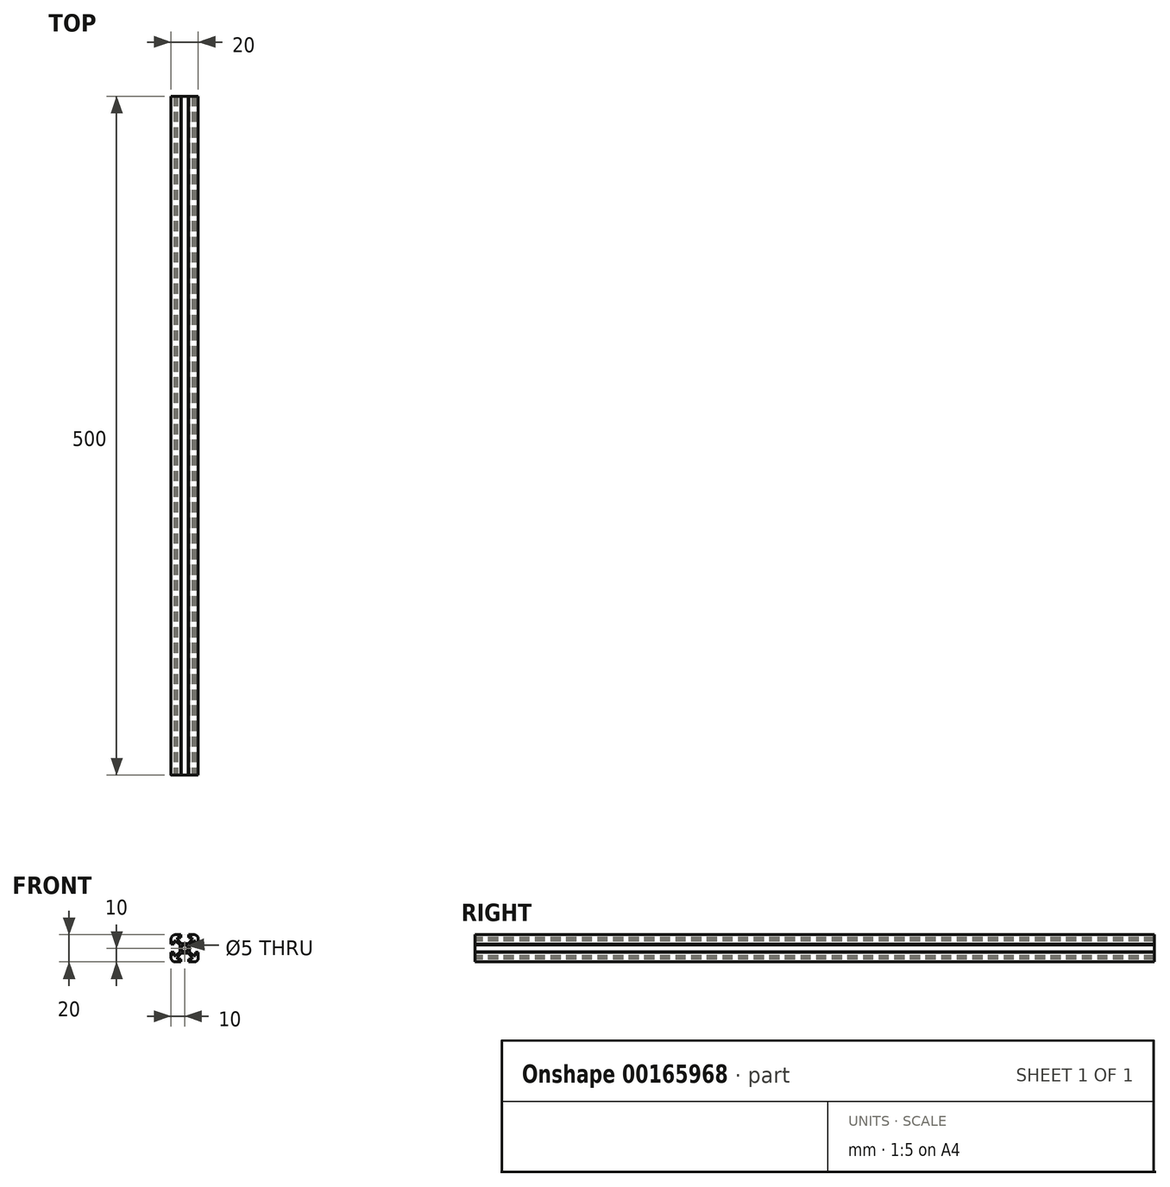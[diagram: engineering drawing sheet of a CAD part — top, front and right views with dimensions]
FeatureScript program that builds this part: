
annotation { "Feature Type Name" : "Feature", "Feature Type Description" : "" }
export const myFeature = defineFeature(function(context is Context, id is Id, definition is map)
    precondition{}
    {
        {
            var Q0;
            Q0=qCreatedBy(makeId("Front.planeOp"),FACE);
            var sketch = newSketch(context, id + "F0", { "sketchPlane" : qUnion([Q0])});
            skCircle(sketch, "E0", {"center": v(0, 0) * mm, "radius": 2.5 * mm});
            skLineSegment(sketch, "E1.bottom", {"start": v(7, -10) * mm, "end": v(3, -10) * mm});
            skLineSegment(sketch, "E1.top", {"start": v(7, 10) * mm, "end": v(3, 10) * mm});
            skLineSegment(sketch, "E1.left", {"start": v(10, -7) * mm, "end": v(10, -3) * mm});
            skLineSegment(sketch, "E1.right", {"start": v(-10, -7) * mm, "end": v(-10, -3) * mm});
            skLineSegment(sketch, "E2.bottom", {"start": v(2.54, -3.6) * mm, "end": v(-2.54, -3.6) * mm});
            skLineSegment(sketch, "E2.top", {"start": v(2.54, 3.6) * mm, "end": v(-2.54, 3.6) * mm});
            skLineSegment(sketch, "E2.left", {"start": v(3.6, -2.54) * mm, "end": v(3.6, 2.54) * mm});
            skLineSegment(sketch, "E2.right", {"start": v(-3.6, -2.54) * mm, "end": v(-3.6, 2.54) * mm});
            skLineSegment(sketch, "E3.bottom", {"start": v(6.94, -8) * mm, "end": v(3, -8) * mm});
            skLineSegment(sketch, "E3.top", {"start": v(6.94, 8) * mm, "end": v(3, 8) * mm});
            skLineSegment(sketch, "E3.left", {"start": v(8, -6.94) * mm, "end": v(8, -3) * mm});
            skLineSegment(sketch, "E3.right", {"start": v(-8, -6.94) * mm, "end": v(-8, -3) * mm});
            skLineSegment(sketch, "E4", {"start": v(-8, 8) * mm, "end": v(8, -8) * mm, "construction": true});
            skLineSegment(sketch, "E5", {"start": v(-8, -8) * mm, "end": v(8, 8) * mm, "construction": true});
            skLineSegment(sketch, "E6", {"start": v(-6.94, 8) * mm, "end": v(-2.54, 3.6) * mm});
            skLineSegment(sketch, "E7", {"start": v(-8, 6.94) * mm, "end": v(-3.6, 2.54) * mm});
            skLineSegment(sketch, "E8", {"start": v(6.94, 8) * mm, "end": v(2.54, 3.6) * mm});
            skLineSegment(sketch, "E9", {"start": v(8, 6.94) * mm, "end": v(3.6, 2.54) * mm});
            skLineSegment(sketch, "E10.trimOffspring", {"start": v(3.6, -2.54) * mm, "end": v(8, -6.94) * mm});
            skLineSegment(sketch, "E11.trimOffspring", {"start": v(2.54, -3.6) * mm, "end": v(6.94, -8) * mm});
            skLineSegment(sketch, "E12.trimOffspring", {"start": v(-2.54, -3.6) * mm, "end": v(-6.94, -8) * mm});
            skLineSegment(sketch, "E13.trimOffspring", {"start": v(-3.6, -2.54) * mm, "end": v(-8, -6.94) * mm});
            skPoint(sketch, "E14.orphan", {"position": v(3.6, 3.6) * mm});
            skPoint(sketch, "E15.orphan", {"position": v(-3.6, 3.6) * mm});
            skPoint(sketch, "E16.orphan", {"position": v(3.6, -3.6) * mm});
            skPoint(sketch, "E17.orphan", {"position": v(-3.6, -3.6) * mm});
            skLineSegment(sketch, "E18", {"start": v(-10, 3) * mm, "end": v(-8, 3) * mm});
            skLineSegment(sketch, "E19.MirrorCS", {"start": v(-10, -3) * mm, "end": v(-8, -3) * mm});
            skLineSegment(sketch, "E20.MirrorCS", {"start": v(10, 3) * mm, "end": v(8, 3) * mm});
            skLineSegment(sketch, "E21.MirrorCS", {"start": v(10, -3) * mm, "end": v(8, -3) * mm});
            skLineSegment(sketch, "E22", {"start": v(-3, 10) * mm, "end": v(-3, 8) * mm});
            skLineSegment(sketch, "E23.MirrorCS", {"start": v(3, 10) * mm, "end": v(3, 8) * mm});
            skLineSegment(sketch, "E24.MirrorCS", {"start": v(3, -10) * mm, "end": v(3, -8) * mm});
            skLineSegment(sketch, "E25.MirrorCS", {"start": v(-3, -10) * mm, "end": v(-3, -8) * mm});
            skLineSegment(sketch, "E26.trimOffspring", {"start": v(-3, 10) * mm, "end": v(-7, 10) * mm});
            skLineSegment(sketch, "E27.trimOffspring", {"start": v(-3, 8) * mm, "end": v(-6.94, 8) * mm});
            skLineSegment(sketch, "E28.trimOffspring", {"start": v(-3, -8) * mm, "end": v(-6.94, -8) * mm});
            skLineSegment(sketch, "E29.trimOffspring", {"start": v(-3, -10) * mm, "end": v(-7, -10) * mm});
            skLineSegment(sketch, "E30.trimOffspring", {"start": v(10, 3) * mm, "end": v(10, 7) * mm});
            skLineSegment(sketch, "E31.trimOffspring", {"start": v(8, 3) * mm, "end": v(8, 6.94) * mm});
            skLineSegment(sketch, "E32.trimOffspring", {"start": v(-8, 3) * mm, "end": v(-8, 6.94) * mm});
            skLineSegment(sketch, "E33.trimOffspring", {"start": v(-10, 3) * mm, "end": v(-10, 7) * mm});
            skPoint(sketch, "E34.visualSharp", {"position": v(-10, 10) * mm});
            skArc(sketch, "E34.filletArc", {"start": v(-7, 10) * mm, "mid": v(-9.12, 9.12) * mm, "end": v(-10, 7) * mm});
            skPoint(sketch, "E35.visualSharp", {"position": v(10, 10) * mm});
            skArc(sketch, "E35.filletArc", {"start": v(10, 7) * mm, "mid": v(9.12, 9.12) * mm, "end": v(7, 10) * mm});
            skPoint(sketch, "E36.visualSharp", {"position": v(10, -10) * mm});
            skArc(sketch, "E36.filletArc", {"start": v(7, -10) * mm, "mid": v(9.12, -9.12) * mm, "end": v(10, -7) * mm});
            skPoint(sketch, "E37.visualSharp", {"position": v(-10, -10) * mm});
            skArc(sketch, "E37.filletArc", {"start": v(-10, -7) * mm, "mid": v(-9.12, -9.12) * mm, "end": v(-7, -10) * mm});
            skLineSegment(sketch, "E38", {"start": v(-5.5, 8) * mm, "end": v(-5.5, 6.56) * mm});
            skLineSegment(sketch, "E39", {"start": v(-8, 5.5) * mm, "end": v(-6.56, 5.5) * mm});
            skLineSegment(sketch, "E40.MirrorCS", {"start": v(5.5, 8) * mm, "end": v(5.5, 6.56) * mm});
            skLineSegment(sketch, "E41.MirrorCS", {"start": v(-5.5, -8) * mm, "end": v(-5.5, -6.56) * mm});
            skLineSegment(sketch, "E42.MirrorCS", {"start": v(-8, -5.5) * mm, "end": v(-6.56, -5.5) * mm});
            skLineSegment(sketch, "E43.MirrorCS", {"start": v(5.5, -8) * mm, "end": v(5.5, -6.56) * mm});
            skLineSegment(sketch, "E44.MirrorCS", {"start": v(8, 5.5) * mm, "end": v(6.56, 5.5) * mm});
            skLineSegment(sketch, "E45.MirrorCS", {"start": v(8, -5.5) * mm, "end": v(6.56, -5.5) * mm});
            skSolve(sketch);
        }
        {
            var Q0;
            Q0 = qSketchRegion(id + "F0", true);
            extrude(context, id + "F1", {"entities" : qUnion([Q0]), "oppositeDirection" : true, "depth" : 500 * mm});
        }
    });
